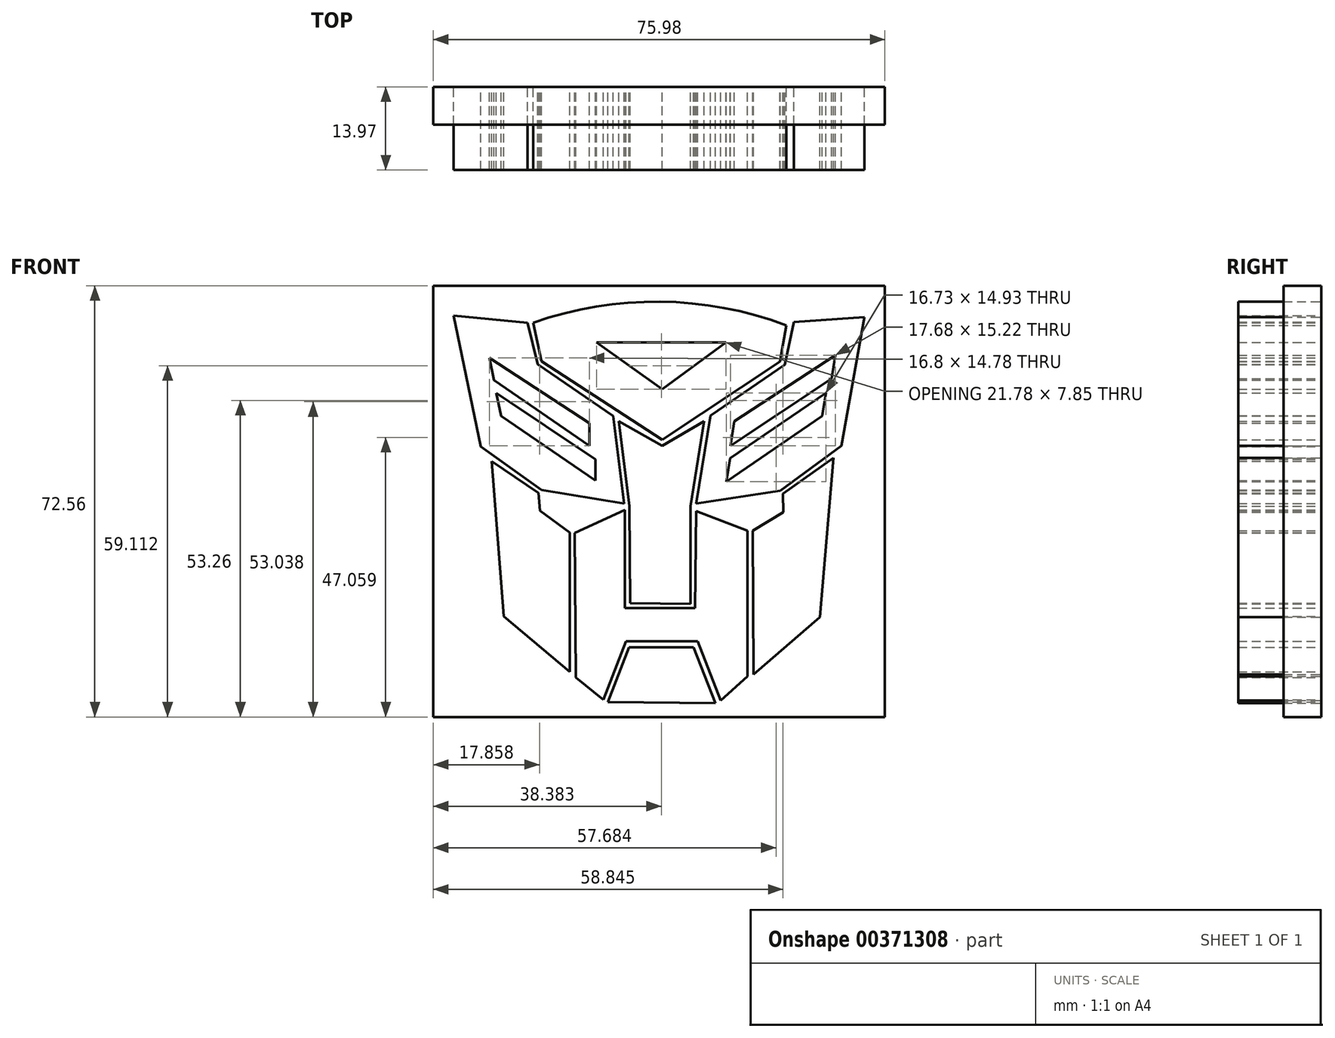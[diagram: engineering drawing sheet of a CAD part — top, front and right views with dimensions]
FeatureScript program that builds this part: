
annotation { "Feature Type Name" : "Feature", "Feature Type Description" : "" }
export const myFeature = defineFeature(function(context is Context, id is Id, definition is map)
    precondition{}
    {
        {
            var Q0;
            Q0=qCreatedBy(makeId("Front.planeOp"),FACE);
            var sketch = newSketch(context, id + "F0", { "sketchPlane" : qUnion([Q0])});
            skLineSegment(sketch, "E0", {"start": v(-22.62, 35) * mm, "end": v(-35.06, 36.21) * mm});
            skLineSegment(sketch, "E1", {"start": v(-35.06, 36.21) * mm, "end": v(-30.54, 14.15) * mm});
            skLineSegment(sketch, "E2", {"start": v(-30.54, 14.15) * mm, "end": v(-20.3, 6.86) * mm});
            skLineSegment(sketch, "E3", {"start": v(-20.3, 6.86) * mm, "end": v(-6.36, 4.6) * mm});
            skLineSegment(sketch, "E4", {"start": v(-6.36, 4.6) * mm, "end": v(-8.23, 19.33) * mm});
            skLineSegment(sketch, "E5", {"start": v(-8.23, 19.33) * mm, "end": v(-20.91, 28.01) * mm});
            skLineSegment(sketch, "E6", {"start": v(-20.91, 28.01) * mm, "end": v(-22.62, 35) * mm});
            skLineSegment(sketch, "E7", {"start": v(-28.86, 11.82) * mm, "end": v(-20.78, 6.35) * mm});
            skLineSegment(sketch, "E8", {"start": v(-20.78, 6.35) * mm, "end": v(-20.55, 3.36) * mm});
            skLineSegment(sketch, "E9", {"start": v(-20.55, 3.36) * mm, "end": v(-15.55, -0.3) * mm});
            skLineSegment(sketch, "E10", {"start": v(-15.55, -0.3) * mm, "end": v(-15.55, -23.77) * mm});
            skLineSegment(sketch, "E11", {"start": v(-15.55, -23.77) * mm, "end": v(-26.62, -14.42) * mm});
            skLineSegment(sketch, "E12", {"start": v(-26.62, -14.42) * mm, "end": v(-28.66, 11.68) * mm});
            skLineSegment(sketch, "E13", {"start": v(-14.68, -0.36) * mm, "end": v(-6.26, 3.49) * mm});
            skLineSegment(sketch, "E14", {"start": v(-6.26, 3.49) * mm, "end": v(-6.26, -13.03) * mm});
            skLineSegment(sketch, "E15", {"start": v(-6.26, -13.03) * mm, "end": v(5.53, -13.03) * mm});
            skLineSegment(sketch, "E16", {"start": v(5.53, -13.03) * mm, "end": v(5.77, 3.3) * mm});
            skLineSegment(sketch, "E17", {"start": v(5.77, 3.3) * mm, "end": v(14.38, 0) * mm});
            skLineSegment(sketch, "E18", {"start": v(14.38, 0) * mm, "end": v(14.38, -24.53) * mm});
            skLineSegment(sketch, "E19", {"start": v(14.38, -24.53) * mm, "end": v(9.9, -28.55) * mm});
            skLineSegment(sketch, "E20", {"start": v(9.9, -28.55) * mm, "end": v(5.99, -18.62) * mm});
            skLineSegment(sketch, "E21", {"start": v(5.99, -18.62) * mm, "end": v(-6.08, -18.62) * mm});
            skLineSegment(sketch, "E22", {"start": v(-6.08, -18.62) * mm, "end": v(-9.86, -28.45) * mm});
            skLineSegment(sketch, "E23", {"start": v(-9.86, -28.45) * mm, "end": v(-14.54, -24.7) * mm});
            skLineSegment(sketch, "E24", {"start": v(-14.54, -24.7) * mm, "end": v(-14.68, -0.36) * mm});
            skLineSegment(sketch, "E25", {"start": v(5.75, 4.6) * mm, "end": v(8.15, 19.37) * mm});
            skLineSegment(sketch, "E26", {"start": v(8.15, 19.37) * mm, "end": v(20.69, 27.93) * mm});
            skLineSegment(sketch, "E27", {"start": v(20.69, 27.93) * mm, "end": v(22.18, 35.1) * mm});
            skLineSegment(sketch, "E28", {"start": v(22.18, 35.1) * mm, "end": v(34.08, 35.97) * mm});
            skLineSegment(sketch, "E29", {"start": v(34.08, 35.97) * mm, "end": v(30.19, 14.26) * mm});
            skLineSegment(sketch, "E30", {"start": v(30.19, 14.26) * mm, "end": v(19.9, 6.76) * mm});
            skLineSegment(sketch, "E31", {"start": v(19.9, 6.76) * mm, "end": v(5.75, 4.6) * mm});
            skLineSegment(sketch, "E32", {"start": v(20.36, 6.22) * mm, "end": v(28.89, 12.24) * mm});
            skLineSegment(sketch, "E33", {"start": v(28.89, 12.24) * mm, "end": v(26.6, -14.57) * mm});
            skLineSegment(sketch, "E34", {"start": v(26.6, -14.57) * mm, "end": v(15.42, -24.2) * mm});
            skLineSegment(sketch, "E35", {"start": v(15.42, -24.2) * mm, "end": v(15.28, 0) * mm});
            skLineSegment(sketch, "E36", {"start": v(15.28, 0) * mm, "end": v(20.39, 3.1) * mm});
            skLineSegment(sketch, "E37", {"start": v(20.36, 6.22) * mm, "end": v(20.39, 3.1) * mm});
            skLineSegment(sketch, "E38", {"start": v(-9.09, -28.83) * mm, "end": v(-5.55, -19.63) * mm});
            skLineSegment(sketch, "E39", {"start": v(-5.55, -19.63) * mm, "end": v(5.31, -19.63) * mm});
            skLineSegment(sketch, "E40", {"start": v(5.31, -19.63) * mm, "end": v(9.01, -29.02) * mm});
            skLineSegment(sketch, "E41", {"start": v(9.01, -29.02) * mm, "end": v(-9.09, -28.83) * mm});
            skLineSegment(sketch, "E42", {"start": v(-29.03, 29.08) * mm, "end": v(-28.32, 25.31) * mm});
            skLineSegment(sketch, "E43", {"start": v(-28.32, 25.31) * mm, "end": v(-12.23, 14.3) * mm});
            skLineSegment(sketch, "E44", {"start": v(-12.23, 14.3) * mm, "end": v(-12.23, 18.09) * mm});
            skLineSegment(sketch, "E45", {"start": v(-12.23, 18.09) * mm, "end": v(-29.03, 29.08) * mm});
            skLineSegment(sketch, "E46", {"start": v(-27.91, 23.18) * mm, "end": v(-27.1, 19.3) * mm});
            skLineSegment(sketch, "E47", {"start": v(-27.1, 19.3) * mm, "end": v(-11.2, 8.42) * mm});
            skLineSegment(sketch, "E48", {"start": v(-11.2, 8.42) * mm, "end": v(-11.2, 11.98) * mm});
            skLineSegment(sketch, "E49", {"start": v(-11.2, 11.98) * mm, "end": v(-27.91, 23.18) * mm});
            skLineSegment(sketch, "E50", {"start": v(11.47, 12.19) * mm, "end": v(10.83, 8.24) * mm});
            skLineSegment(sketch, "E51", {"start": v(10.83, 8.24) * mm, "end": v(26.93, 19.3) * mm});
            skLineSegment(sketch, "E52", {"start": v(26.93, 19.3) * mm, "end": v(27.56, 23.18) * mm});
            skLineSegment(sketch, "E53", {"start": v(27.56, 23.18) * mm, "end": v(11.47, 12.19) * mm});
            skLineSegment(sketch, "E54", {"start": v(12.18, 18.4) * mm, "end": v(11.51, 14.3) * mm});
            skLineSegment(sketch, "E55", {"start": v(11.51, 14.3) * mm, "end": v(28.56, 25.62) * mm});
            skLineSegment(sketch, "E56", {"start": v(28.56, 25.62) * mm, "end": v(29.2, 29.52) * mm});
            skLineSegment(sketch, "E57", {"start": v(29.2, 29.52) * mm, "end": v(12.18, 18.4) * mm});
            skLineSegment(sketch, "E58", {"start": v(-7.3, 18.4) * mm, "end": v(-5.49, 4.15) * mm});
            skPoint(sketch, "E58.startSnap0", {"position": v(-7.3, 11.96) * mm});
            skLineSegment(sketch, "E59", {"start": v(-5.49, 4.15) * mm, "end": v(-5.4, -12.2) * mm});
            skLineSegment(sketch, "E60", {"start": v(-5.4, -12.2) * mm, "end": v(4.77, -12.34) * mm});
            skLineSegment(sketch, "E61", {"start": v(4.77, -12.34) * mm, "end": v(4.77, 4.15) * mm});
            skLineSegment(sketch, "E62", {"start": v(4.77, 4.15) * mm, "end": v(7.08, 18.4) * mm});
            skLineSegment(sketch, "E63", {"start": v(7.08, 18.4) * mm, "end": v(0, 14.3) * mm});
            skLineSegment(sketch, "E64", {"start": v(0, 14.3) * mm, "end": v(-7.3, 18.4) * mm});
            skLineSegment(sketch, "E65", {"start": v(-21.65, 35) * mm, "end": v(-20.26, 28.5) * mm});
            skLineSegment(sketch, "E66", {"start": v(-20.26, 28.5) * mm, "end": v(0, 15.3) * mm});
            skLineSegment(sketch, "E67", {"start": v(0, 15.3) * mm, "end": v(19.82, 28.46) * mm});
            skLineSegment(sketch, "E68", {"start": v(19.82, 28.46) * mm, "end": v(20.91, 34.56) * mm});
            skArc(sketch, "E69", {"start": v(20.91, 34.56) * mm, "mid": v(-0.33, 38.54) * mm, "end": v(-21.65, 35) * mm});
            skLineSegment(sketch, "E70", {"start": v(-11, 31.69) * mm, "end": v(10.78, 31.69) * mm});
            skLineSegment(sketch, "E71", {"start": v(10.78, 31.69) * mm, "end": v(0, 23.84) * mm});
            skLineSegment(sketch, "E72", {"start": v(0, 23.84) * mm, "end": v(-11, 31.69) * mm});
            skSolve(sketch);
        }
        {
            var Q0;
            Q0 = qSketchRegion(id + "F0", true);
            extrude(context, id + "F1", {"entities" : qUnion([Q0]), "depth" : 13.97 * mm});
        }
        {
            var Q0;
            Q0=qCreatedBy(makeId("Front.planeOp"),FACE);
            var sketch = newSketch(context, id + "F2", { "sketchPlane" : qUnion([Q0])});
            skLineSegment(sketch, "E73.bottom", {"start": v(37.5, 41.21) * mm, "end": v(-38.49, 41.21) * mm});
            skLineSegment(sketch, "E73.top", {"start": v(37.5, -31.35) * mm, "end": v(-38.49, -31.35) * mm});
            skLineSegment(sketch, "E73.left", {"start": v(37.5, 41.21) * mm, "end": v(37.5, -31.35) * mm});
            skLineSegment(sketch, "E73.right", {"start": v(-38.49, 41.21) * mm, "end": v(-38.49, -31.35) * mm});
            skSolve(sketch);
        }
        {
            var Q0;
            Q0 = qSketchRegion(id + "F2", true);
            extrude(context, id + "F3", {"entities" : qUnion([Q0]), "depth" : 6.35 * mm});
        }
    });
